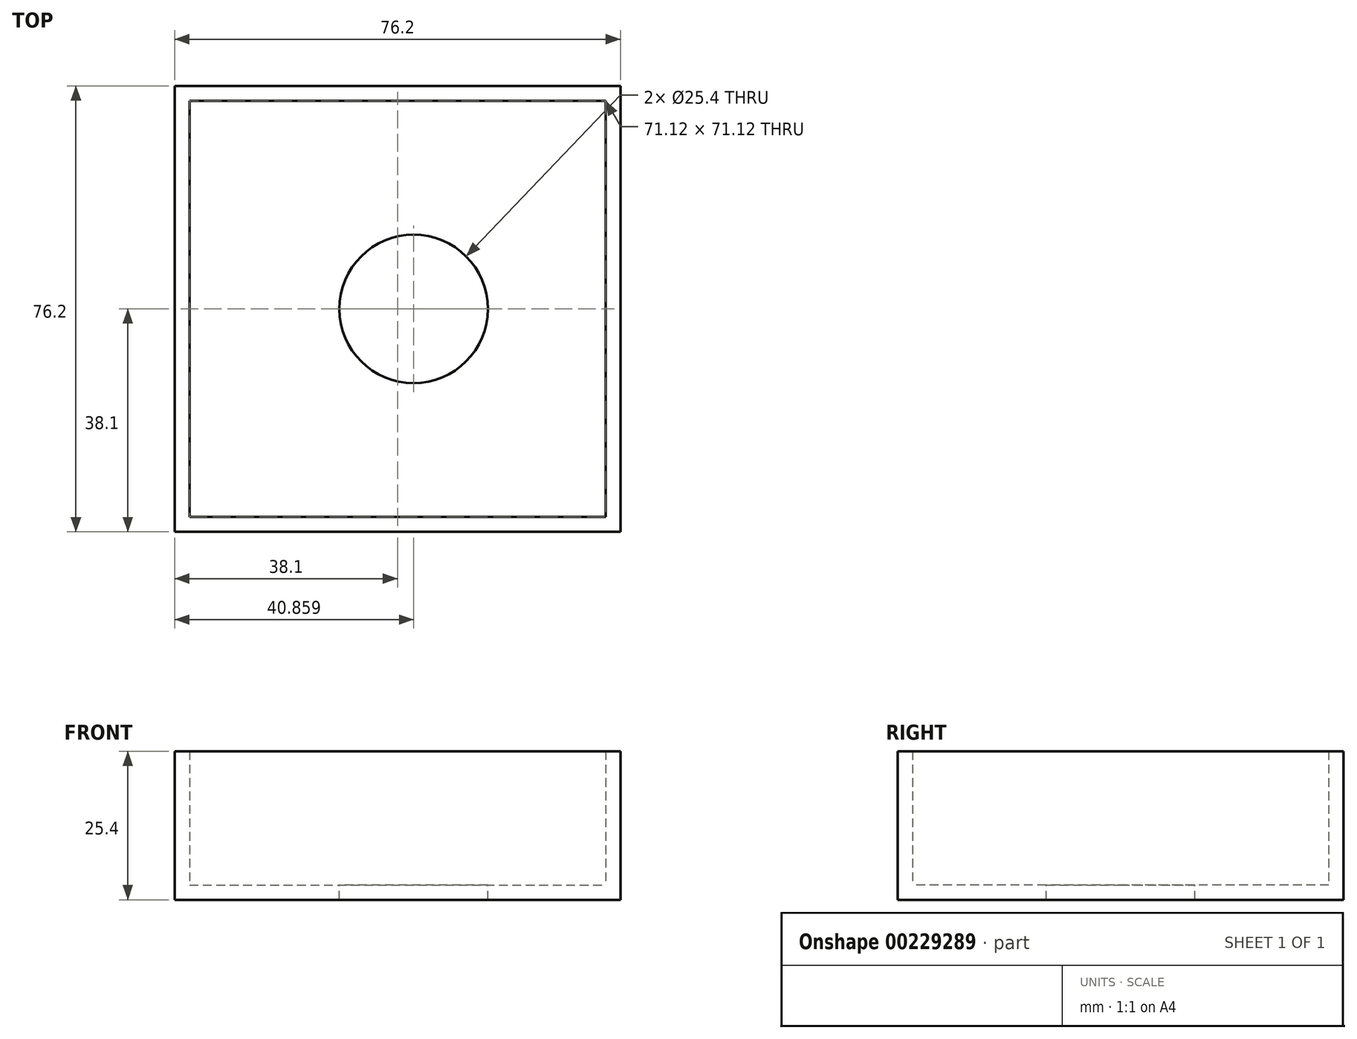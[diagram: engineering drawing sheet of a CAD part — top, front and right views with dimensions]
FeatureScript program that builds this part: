
annotation { "Feature Type Name" : "Feature", "Feature Type Description" : "" }
export const myFeature = defineFeature(function(context is Context, id is Id, definition is map)
    precondition{}
    {
        {
            var Q0;
            Q0=qCreatedBy(makeId("Top.planeOp"),FACE);
            var sketch = newSketch(context, id + "F0", { "sketchPlane" : qUnion([Q0])});
            skLineSegment(sketch, "E0.bottom", {"start": v(-38.1, 38.1) * mm, "end": v(38.1, 38.1) * mm});
            skLineSegment(sketch, "E0.top", {"start": v(-38.1, -38.1) * mm, "end": v(38.1, -38.1) * mm});
            skLineSegment(sketch, "E0.left", {"start": v(-38.1, 38.1) * mm, "end": v(-38.1, -38.1) * mm});
            skLineSegment(sketch, "E0.right", {"start": v(38.1, 38.1) * mm, "end": v(38.1, -38.1) * mm});
            skSolve(sketch);
        }
        {
            var Q0;
            Q0 = qSketchRegion(id + "F0", true);
            extrude(context, id + "F1", {"entities" : qUnion([Q0]), "depth" : 25.4 * mm});
        }
        {
            var Q0;
            Q0=makeQuery(id+"F1.opExtrude","CAP_FACE",FACE,{"disambiguationData":[OSD([sQuery(id+"F0.wireOp",EDGE,"E0.bottom"),sQuery(id+"F0.wireOp",EDGE,"E0.top"),sQuery(id+"F0.wireOp",EDGE,"E0.left"),sQuery(id+"F0.wireOp",EDGE,"E0.right")])],"isStart":false});
            shell(context, id + "F2", {"entities" : qUnion([Q0]), "thickness" : 2.54 * mm});
        }
        {
            var Q0;
            Q0=makeQuery(id+"F2.opShell","OFFSET_FACE",FACE,{"disambiguationData":[OSD([sQuery(id+"F0.wireOp",EDGE,"E0.bottom"),sQuery(id+"F0.wireOp",EDGE,"E0.top"),sQuery(id+"F0.wireOp",EDGE,"E0.left"),sQuery(id+"F0.wireOp",EDGE,"E0.right")])]});
            var sketch = newSketch(context, id + "F3", { "sketchPlane" : qUnion([Q0])});
            skCircle(sketch, "E1", {"center": v(2.76, 0) * mm, "radius": 13.44 * mm});
            skSolve(sketch);
        }
        {
            var Q0;
            Q0=sQuery(id+"F3.wireOp",VERTEX,"E1.center");
            var Q1;
            Q1=makeQuery(id+"F1.opExtrude","SWEPT_BODY",BODY,{"disambiguationData":[OSD([sQuery(id+"F0.wireOp",EDGE,"E0.bottom"),sQuery(id+"F0.wireOp",EDGE,"E0.top"),sQuery(id+"F0.wireOp",EDGE,"E0.left"),sQuery(id+"F0.wireOp",EDGE,"E0.right")])]});
            hole(context, id + "F4", {"style" : HoleStyle.SIMPLE, "endStyle" : HoleEndStyle.THROUGH, "holeDiameter" : 25.4 * mm, "locations" : qUnion([Q0]), "scope" : qUnion([Q1]), "isTappedThrough" : true});
        }
        {
            var Q0;
            Q0=makeQuery(id+"F1.opExtrude","SWEPT_BODY",BODY,{"disambiguationData":[OSD([sQuery(id+"F0.wireOp",EDGE,"E0.bottom"),sQuery(id+"F0.wireOp",EDGE,"E0.top"),sQuery(id+"F0.wireOp",EDGE,"E0.left"),sQuery(id+"F0.wireOp",EDGE,"E0.right")])]});
            transform(context, id + "F5", {"entities" : qUnion([Q0]), "transformType" : TransformType.TRANSLATION_3D, "dx" : 0 * mm, "dy" : 0 * mm, "dz" : 0 * mm, "makeCopy" : true});
        }
    });
